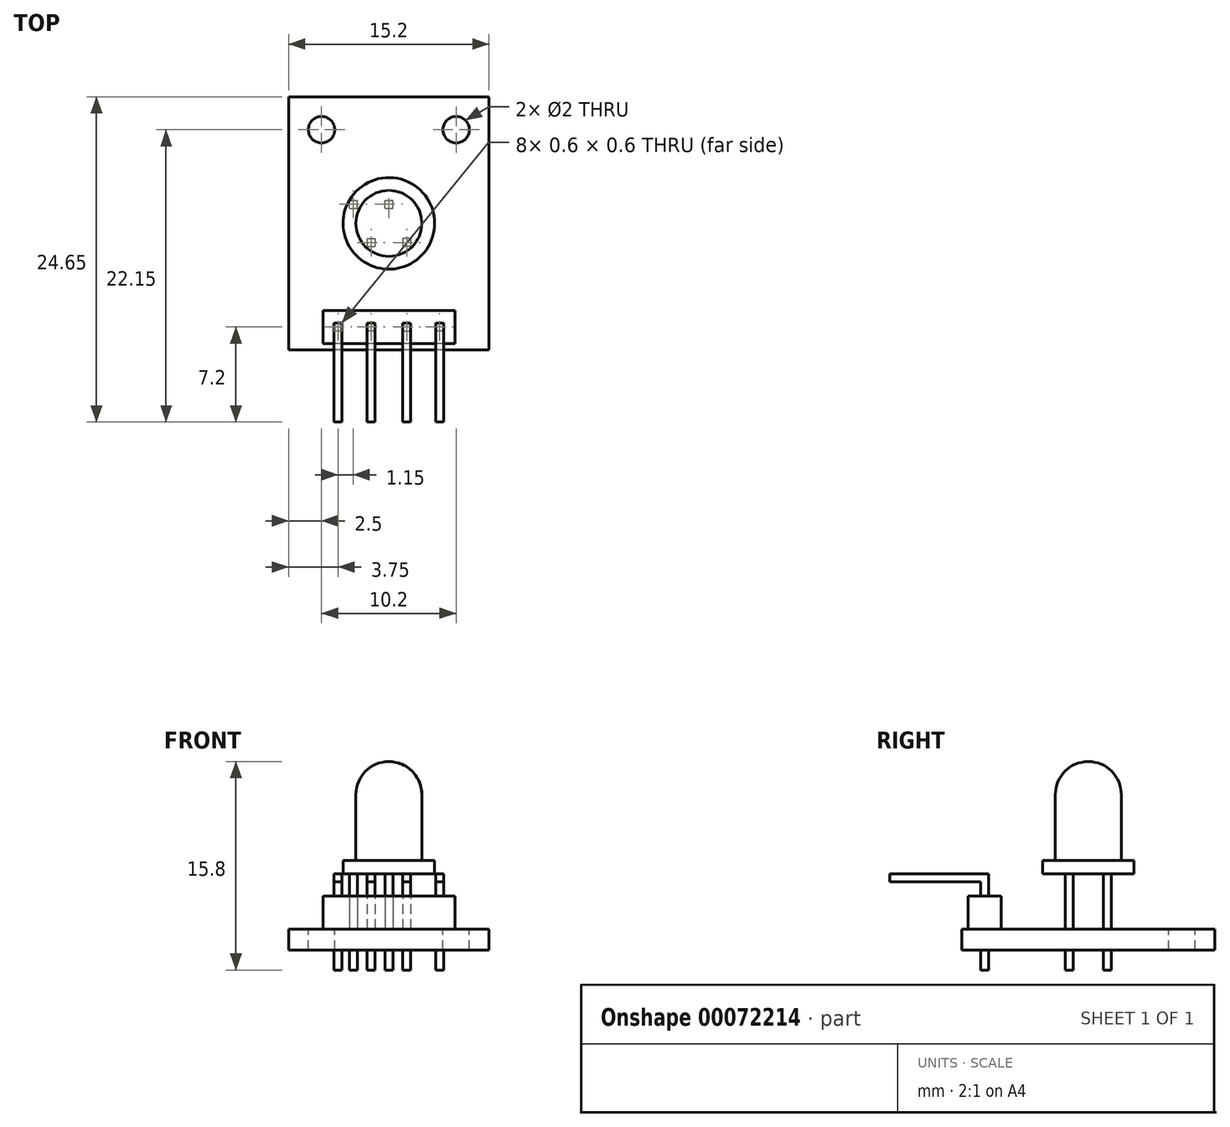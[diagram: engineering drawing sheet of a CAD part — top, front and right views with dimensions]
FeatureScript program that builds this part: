
annotation { "Feature Type Name" : "Feature", "Feature Type Description" : "" }
export const myFeature = defineFeature(function(context is Context, id is Id, definition is map)
    precondition{}
    {
        {
            var Q0;
            Q0=qCreatedBy(makeId("Top.planeOp"),FACE);
            var sketch = newSketch(context, id + "F0", { "sketchPlane" : qUnion([Q0])});
            skLineSegment(sketch, "E0.rect.bottom", {"start": v(7.6, 9.6) * mm, "end": v(-7.6, 9.6) * mm});
            skLineSegment(sketch, "E0.rect.top", {"start": v(7.6, -9.6) * mm, "end": v(-7.6, -9.6) * mm});
            skLineSegment(sketch, "E0.rect.left", {"start": v(7.6, 9.6) * mm, "end": v(7.6, -9.6) * mm});
            skLineSegment(sketch, "E0.rect.right", {"start": v(-7.6, 9.6) * mm, "end": v(-7.6, -9.6) * mm});
            skPoint(sketch, "E0.rect.middle", {"position": v(0, 0) * mm});
            skSolve(sketch);
        }
        {
            var Q0;
            Q0=qSketchRegion(id+"F0",true);
            extrude(context, id + "F1", {"entities" : qUnion([Q0]), "depth" : 1.6 * mm});
        }
        {
            var Q0;
            Q0=makeQuery(id+"F1.opExtrude","CAP_FACE",FACE,{"disambiguationData":[OSD([sQuery(id+"F0.wireOp",EDGE,"E0.rect.bottom"),sQuery(id+"F0.wireOp",EDGE,"E0.rect.top"),sQuery(id+"F0.wireOp",EDGE,"E0.rect.left"),sQuery(id+"F0.wireOp",EDGE,"E0.rect.right")])],"isStart":false});
            var sketch = newSketch(context, id + "F2", { "sketchPlane" : qUnion([Q0])});
            skCircle(sketch, "E1", {"center": v(-5.1, 7.1) * mm, "radius": 1 * mm});
            skCircle(sketch, "E2.MirrorC", {"center": v(5.1, 7.1) * mm, "radius": 1 * mm});
            skSolve(sketch);
        }
        {
            var Q0;
            Q0=qSketchRegion(id+"F2",true);
            extrude(context, id + "F3", {"entities" : qUnion([Q0]), "operationType" : NewBodyOperationType.REMOVE, "oppositeDirection" : true, "depth" : 25 * mm});
        }
        {
            var Q0;
            Q0=makeQuery(id+"F1.opExtrude","CAP_FACE",FACE,{"disambiguationData":[OSD([sQuery(id+"F0.wireOp",EDGE,"E0.rect.bottom"),sQuery(id+"F0.wireOp",EDGE,"E0.rect.top"),sQuery(id+"F0.wireOp",EDGE,"E0.rect.left"),sQuery(id+"F0.wireOp",EDGE,"E0.rect.right")])],"isStart":false});
            var sketch = newSketch(context, id + "F4", { "sketchPlane" : qUnion([Q0])});
            skLineSegment(sketch, "E3.rect.bottom", {"start": v(5, -6.6) * mm, "end": v(-5, -6.6) * mm});
            skLineSegment(sketch, "E3.rect.top", {"start": v(5, -9.1) * mm, "end": v(-5, -9.1) * mm});
            skLineSegment(sketch, "E3.rect.left", {"start": v(5, -6.6) * mm, "end": v(5, -9.1) * mm});
            skLineSegment(sketch, "E3.rect.right", {"start": v(-5, -6.6) * mm, "end": v(-5, -9.1) * mm});
            skPoint(sketch, "E3.rect.middle", {"position": v(0, -7.85) * mm});
            skSolve(sketch);
        }
        {
            var Q0;
            Q0=qSketchRegion(id+"F4",true);
            extrude(context, id + "F5", {"entities" : qUnion([Q0]), "operationType" : NewBodyOperationType.ADD, "depth" : 2.5 * mm});
        }
        {
            var Q0;
            Q0=qCreatedBy(makeId("Top.planeOp"),FACE);
            cPlane(context, id + "F6", {"entities" : qUnion([Q0]), "cplaneType" : CPlaneType.OFFSET, "offset" : 1.5 * mm, "oppositeDirection" : true, "width" : 150 * mm, "height" : 150 * mm});
        }
        {
            var Q0;
            Q0=qCreatedBy(id+"F6.planeOp",FACE);
            var sketch = newSketch(context, id + "F7", { "sketchPlane" : qUnion([Q0])});
            skLineSegment(sketch, "E4.1.0.0", {"start": v(4.15, -7.55) * mm, "end": v(4.15, -8.15) * mm});
            skLineSegment(sketch, "E4.1.0.1", {"start": v(3.55, -8.15) * mm, "end": v(4.15, -8.15) * mm});
            skLineSegment(sketch, "E4.1.0.2", {"start": v(3.55, -7.55) * mm, "end": v(3.55, -8.15) * mm});
            skLineSegment(sketch, "E4.1.0.3", {"start": v(3.55, -7.55) * mm, "end": v(4.15, -7.55) * mm});
            skLineSegment(sketch, "E5.MirrorCS", {"start": v(-3.55, -7.55) * mm, "end": v(-3.55, -8.15) * mm});
            skLineSegment(sketch, "E6.MirrorCS", {"start": v(-4.15, -7.55) * mm, "end": v(-4.15, -8.15) * mm});
            skLineSegment(sketch, "E7.MirrorCS", {"start": v(-3.55, -7.55) * mm, "end": v(-4.15, -7.55) * mm});
            skLineSegment(sketch, "E8.MirrorCS", {"start": v(-3.55, -8.15) * mm, "end": v(-4.15, -8.15) * mm});
            skLineSegment(sketch, "E9", {"start": v(-5, -7.85) * mm, "end": v(5, -7.85) * mm, "construction": true});
            skPoint(sketch, "E10", {"position": v(-3.55, -7.85) * mm});
            skLineSegment(sketch, "E11.rect.bottom", {"start": v(-1.05, -7.55) * mm, "end": v(-1.65, -7.55) * mm});
            skLineSegment(sketch, "E11.rect.top", {"start": v(-1.05, -8.15) * mm, "end": v(-1.65, -8.15) * mm});
            skLineSegment(sketch, "E11.rect.left", {"start": v(-1.05, -7.55) * mm, "end": v(-1.05, -8.15) * mm});
            skLineSegment(sketch, "E11.rect.right", {"start": v(-1.65, -7.55) * mm, "end": v(-1.65, -8.15) * mm});
            skPoint(sketch, "E11.rect.middle", {"position": v(-1.35, -7.85) * mm});
            skLineSegment(sketch, "E12.MirrorCS", {"start": v(1.05, -8.15) * mm, "end": v(1.65, -8.15) * mm});
            skLineSegment(sketch, "E13.MirrorCS", {"start": v(1.65, -7.55) * mm, "end": v(1.65, -8.15) * mm});
            skLineSegment(sketch, "E14.MirrorCS", {"start": v(1.05, -7.55) * mm, "end": v(1.65, -7.55) * mm});
            skLineSegment(sketch, "E15.MirrorCS", {"start": v(1.05, -7.55) * mm, "end": v(1.05, -8.15) * mm});
            skLineSegment(sketch, "E16", {"start": v(0, -4.65) * mm, "end": v(5.32, -4.65) * mm, "construction": true});
            skLineSegment(sketch, "E17.MirrorCS", {"start": v(1.05, -1.75) * mm, "end": v(1.65, -1.75) * mm});
            skLineSegment(sketch, "E18.MirrorCS", {"start": v(1.05, -1.75) * mm, "end": v(1.05, -1.15) * mm});
            skLineSegment(sketch, "E19.MirrorCS", {"start": v(1.05, -1.15) * mm, "end": v(1.65, -1.15) * mm});
            skLineSegment(sketch, "E20.MirrorCS", {"start": v(1.65, -1.75) * mm, "end": v(1.65, -1.15) * mm});
            skLineSegment(sketch, "E21.MirrorCS", {"start": v(-1.65, -1.75) * mm, "end": v(-1.65, -1.15) * mm});
            skLineSegment(sketch, "E22.MirrorCS", {"start": v(-1.05, -1.75) * mm, "end": v(-1.65, -1.75) * mm});
            skLineSegment(sketch, "E23.MirrorCS", {"start": v(-1.05, -1.15) * mm, "end": v(-1.65, -1.15) * mm});
            skLineSegment(sketch, "E24.MirrorCS", {"start": v(-1.05, -1.75) * mm, "end": v(-1.05, -1.15) * mm});
            skLineSegment(sketch, "E25.rect.bottom", {"start": v(0.3, 1.75) * mm, "end": v(-0.3, 1.75) * mm});
            skLineSegment(sketch, "E25.rect.top", {"start": v(0.3, 1.15) * mm, "end": v(-0.3, 1.15) * mm});
            skLineSegment(sketch, "E25.rect.left", {"start": v(0.3, 1.75) * mm, "end": v(0.3, 1.15) * mm});
            skLineSegment(sketch, "E25.rect.right", {"start": v(-0.3, 1.75) * mm, "end": v(-0.3, 1.15) * mm});
            skPoint(sketch, "E25.rect.middle", {"position": v(0, 1.45) * mm});
            skLineSegment(sketch, "E26.rect.bottom", {"start": v(-2.4, 1.75) * mm, "end": v(-3, 1.75) * mm});
            skLineSegment(sketch, "E26.rect.top", {"start": v(-2.4, 1.15) * mm, "end": v(-3, 1.15) * mm});
            skLineSegment(sketch, "E26.rect.left", {"start": v(-2.4, 1.75) * mm, "end": v(-2.4, 1.15) * mm});
            skLineSegment(sketch, "E26.rect.right", {"start": v(-3, 1.75) * mm, "end": v(-3, 1.15) * mm});
            skPoint(sketch, "E26.rect.middle", {"position": v(-2.7, 1.45) * mm});
            skPoint(sketch, "E26.rect.middle.positionSnap0", {"position": v(-0.3, 1.45) * mm});
            skPoint(sketch, "E26.rect.centerSnap0", {"position": v(-0.3, 1.45) * mm});
            skLineSegment(sketch, "E27", {"start": v(1.05, -1.75) * mm, "end": v(-1.05, -1.75) * mm, "construction": true});
            skLineSegment(sketch, "E28", {"start": v(-0.3, 1.15) * mm, "end": v(-2.4, 1.15) * mm, "construction": true});
            skSolve(sketch);
        }
        {
            var Q0;
            Q0=qSketchRegion(id+"F7",true);
            extrude(context, id + "F8", {"entities" : qUnion([Q0]), "operationType" : NewBodyOperationType.ADD, "depth" : 7.3 * mm});
        }
        {
            var Q0;
            {var subQ2=sQuery(id+"F7.wireOp",EDGE,"E7.MirrorCS");Q0=makeQuery(id+"F8.boolean.opBoolean","SPLIT",FACE,{"disambiguationData":[TD([makeQuery(id+"F5.opExtrude","CAP_FACE",FACE,{"disambiguationData":[OSD([sQuery(id+"F4.wireOp",EDGE,"E3.rect.bottom"),sQuery(id+"F4.wireOp",EDGE,"E3.rect.top"),sQuery(id+"F4.wireOp",EDGE,"E3.rect.left"),sQuery(id+"F4.wireOp",EDGE,"E3.rect.right")])],"isStart":false})])],"derivedFrom":makeQuery(id+"F8.opExtrude","SWEPT_FACE",FACE,{"disambiguationData":[OSD([subQ2])]})});}
            var sketch = newSketch(context, id + "F9", { "sketchPlane" : qUnion([Q0])});
            skLineSegment(sketch, "E29.bottom", {"start": v(4.15, 5.8) * mm, "end": v(3.55, 5.8) * mm});
            skLineSegment(sketch, "E29.top", {"start": v(4.15, 5.2) * mm, "end": v(3.55, 5.2) * mm});
            skLineSegment(sketch, "E29.left", {"start": v(4.15, 5.8) * mm, "end": v(4.15, 5.2) * mm});
            skLineSegment(sketch, "E29.right", {"start": v(3.55, 5.8) * mm, "end": v(3.55, 5.2) * mm});
            skLineSegment(sketch, "E30.MirrorCS", {"start": v(-4.15, 5.8) * mm, "end": v(-4.15, 5.2) * mm});
            skLineSegment(sketch, "E31.MirrorCS", {"start": v(-4.15, 5.2) * mm, "end": v(-3.55, 5.2) * mm});
            skLineSegment(sketch, "E32.MirrorCS", {"start": v(-3.55, 5.8) * mm, "end": v(-3.55, 5.2) * mm});
            skLineSegment(sketch, "E33.MirrorCS", {"start": v(-4.15, 5.8) * mm, "end": v(-3.55, 5.8) * mm});
            skLineSegment(sketch, "E34.bottom", {"start": v(1.65, 5.8) * mm, "end": v(1.05, 5.8) * mm});
            skLineSegment(sketch, "E34.top", {"start": v(1.65, 5.2) * mm, "end": v(1.05, 5.2) * mm});
            skLineSegment(sketch, "E34.left", {"start": v(1.65, 5.8) * mm, "end": v(1.65, 5.2) * mm});
            skLineSegment(sketch, "E34.right", {"start": v(1.05, 5.8) * mm, "end": v(1.05, 5.2) * mm});
            skLineSegment(sketch, "E35.bottom", {"start": v(-1.05, 5.8) * mm, "end": v(-1.65, 5.8) * mm});
            skLineSegment(sketch, "E35.top", {"start": v(-1.05, 5.2) * mm, "end": v(-1.65, 5.2) * mm});
            skLineSegment(sketch, "E35.left", {"start": v(-1.05, 5.8) * mm, "end": v(-1.05, 5.2) * mm});
            skLineSegment(sketch, "E35.right", {"start": v(-1.65, 5.8) * mm, "end": v(-1.65, 5.2) * mm});
            skSolve(sketch);
        }
        {
            var Q0;
            Q0=qSketchRegion(id+"F9",true);
            extrude(context, id + "F10", {"entities" : qUnion([Q0]), "operationType" : NewBodyOperationType.ADD, "oppositeDirection" : true, "depth" : 7.5 * mm});
        }
        {
            var Q0;
            Q0=makeQuery(id+"F8.opExtrude","CAP_FACE",FACE,{"disambiguationData":[OSD([sQuery(id+"F7.wireOp",EDGE,"E17.MirrorCS"),sQuery(id+"F7.wireOp",EDGE,"E18.MirrorCS"),sQuery(id+"F7.wireOp",EDGE,"E19.MirrorCS"),sQuery(id+"F7.wireOp",EDGE,"E20.MirrorCS")])],"isStart":false});
            var sketch = newSketch(context, id + "F11", { "sketchPlane" : qUnion([Q0])});
            skCircle(sketch, "E36", {"center": v(0, 0) * mm, "radius": 3.47 * mm});
            skSolve(sketch);
        }
        {
            var Q0;
            Q0=qSketchRegion(id+"F11",true);
            extrude(context, id + "F12", {"entities" : qUnion([Q0]), "operationType" : NewBodyOperationType.ADD, "depth" : 1 * mm});
        }
        {
            var Q0;
            Q0=makeQuery(id+"F12.opExtrude","CAP_FACE",FACE,{"disambiguationData":[OSD([sQuery(id+"F11.wireOp",EDGE,"E36")])],"isStart":false});
            var sketch = newSketch(context, id + "F13", { "sketchPlane" : qUnion([Q0])});
            skCircle(sketch, "E37", {"center": v(0, 0) * mm, "radius": 2.5 * mm});
            skSolve(sketch);
        }
        {
            var Q0;
            Q0=qSketchRegion(id+"F13",true);
            extrude(context, id + "F14", {"entities" : qUnion([Q0]), "operationType" : NewBodyOperationType.ADD, "depth" : 7.5 * mm});
        }
        {
            var Q0;
            Q0=makeQuery(id+"F14.opExtrude","CAP_EDGE",EDGE,{"disambiguationData":[OSD([sQuery(id+"F13.wireOp",EDGE,"E37")])],"isStart":false});
            fillet(context, id + "F15", {"entities" : qUnion([Q0]), "radius" : 2.5 * mm, "tangentPropagation" : true, "allowEdgeOverflow" : false});
        }
    });
